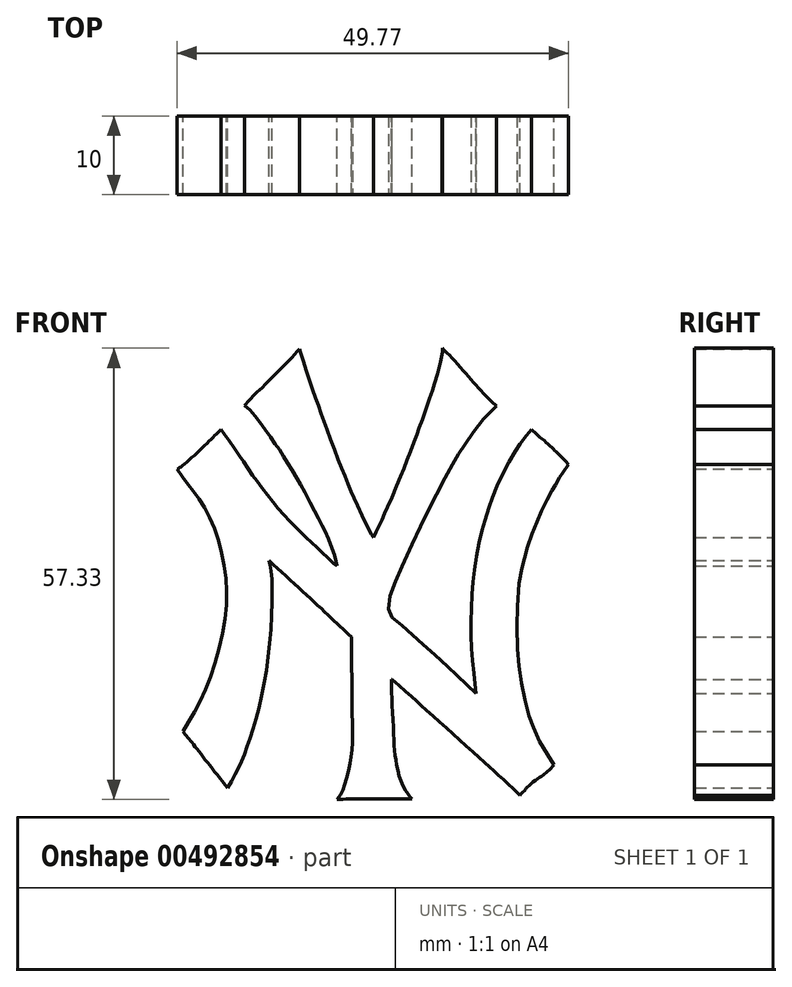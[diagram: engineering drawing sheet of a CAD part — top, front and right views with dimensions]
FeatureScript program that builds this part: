
annotation { "Feature Type Name" : "Feature", "Feature Type Description" : "" }
export const myFeature = defineFeature(function(context is Context, id is Id, definition is map)
    precondition{}
    {
        {
            var Q0;
            Q0=qCreatedBy(makeId("Front.planeOp"),FACE);
            var sketch = newSketch(context, id + "F0", { "sketchPlane" : qUnion([Q0])});
            skFitSpline(sketch, "E0", {"points": [v(5.8, 47.07) * mm, v(6.29, 46.4) * mm, v(7.13, 45.23) * mm, v(8.19, 43.72) * mm, v(8.73, 42.93) * mm, v(9.6, 41.61) * mm, v(10.3, 40.65) * mm, v(11.14, 39.47) * mm, v(12.2, 38.1) * mm, v(13.16, 36.97) * mm, v(14.22, 35.8) * mm, v(15.06, 34.9) * mm, v(15.95, 34) * mm, v(16.93, 33.02) * mm, v(17.78, 32.26) * mm, v(18.71, 31.4) * mm, v(19.49, 30.65) * mm, v(20.36, 29.84) * mm, v(20.56, 29.7) * mm], "startDerivative": vector(7.77, -16.64) * mm, "endDerivative": vector(6.87, -3.56) * mm});
            skFitSpline(sketch, "E1", {"points": [v(20.56, 29.7) * mm, v(20.5, 30.1) * mm, v(20.25, 30.98) * mm, v(19.9, 32.05) * mm, v(19.1, 33.94) * mm, v(18.74, 34.72) * mm, v(18.1, 36) * mm, v(17.32, 37.47) * mm, v(16.13, 39.67) * mm, v(15.54, 40.7) * mm, v(14.54, 42.37) * mm, v(13.92, 43.4) * mm, v(13.19, 44.57) * mm, v(12.51, 45.52) * mm, v(11.5, 47) * mm, v(10.53, 48.24) * mm, v(9.66, 49.36) * mm, v(8.8, 50.14) * mm], "startDerivative": vector(-1.03, 10.89) * mm, "endDerivative": vector(-16.3, 14.17) * mm});
            skFitSpline(sketch, "E2", {"points": [v(8.8, 50.14) * mm, v(9.3, 50.67) * mm, v(10.05, 51.48) * mm, v(11.26, 52.6) * mm, v(13.17, 54.56) * mm, v(14.9, 56.3) * mm, v(15.77, 57.29) * mm, v(15.78, 57.28) * mm], "startDerivative": vector(4.68, 3.9) * mm, "endDerivative": vector(0.38, -0.96) * mm});
            skFitSpline(sketch, "E3", {"points": [v(15.78, 57.28) * mm, v(15.97, 56.7) * mm, v(16.36, 55.47) * mm, v(16.94, 53.7) * mm, v(17.7, 51.47) * mm, v(18.17, 50.1) * mm, v(18.67, 48.69) * mm, v(19.2, 47.22) * mm, v(20.08, 44.92) * mm, v(20.9, 42.77) * mm, v(21.52, 41.23) * mm, v(22.14, 39.73) * mm, v(22.6, 38.62) * mm, v(23.2, 37.29) * mm, v(24.37, 34.84) * mm, v(25.12, 33.43) * mm, v(25.16, 33.38) * mm, v(25.2, 33.37) * mm], "startDerivative": vector(4.56, -13.3) * mm, "endDerivative": vector(1.36, -3.09) * mm});
            skFitSpline(sketch, "E4", {"points": [v(25.2, 33.37) * mm, v(25.59, 34.14) * mm, v(26.08, 35.18) * mm, v(26.53, 36.22) * mm, v(27.1, 37.44) * mm, v(28.39, 40.5) * mm, v(29.14, 42.35) * mm, v(29.9, 44.3) * mm, v(30.64, 46.27) * mm, v(31.03, 47.35) * mm, v(31.94, 49.9) * mm, v(32.7, 52.07) * mm, v(33.1, 53.45) * mm, v(33.91, 56.67) * mm, v(33.91, 57.37) * mm, v(33.92, 57.4) * mm], "startDerivative": vector(7.42, 14.98) * mm, "endDerivative": vector(0.15, 2.07) * mm});
            skFitSpline(sketch, "E5", {"points": [v(33.92, 57.4) * mm, v(34.4, 56.96) * mm, v(35.8, 55.45) * mm, v(37.46, 53.57) * mm, v(38.85, 51.99) * mm, v(40.17, 50.62) * mm, v(40.82, 50.06) * mm], "startDerivative": vector(3.8, -3.56) * mm, "endDerivative": vector(4.92, -3.97) * mm});
            skFitSpline(sketch, "E6", {"points": [v(40.82, 50.06) * mm, v(39.4, 48.66) * mm, v(38.91, 48.1) * mm, v(37.95, 46.84) * mm, v(37.23, 45.77) * mm, v(36.72, 45.03) * mm, v(36.41, 44.52) * mm, v(36.04, 44) * mm, v(35.71, 43.4) * mm, v(35.32, 42.78) * mm, v(34.94, 42.07) * mm, v(34.23, 40.88) * mm, v(33.53, 39.5) * mm, v(32.67, 37.88) * mm, v(32.1, 36.75) * mm, v(31.56, 35.57) * mm, v(30.39, 33.23) * mm, v(29.9, 32.1) * mm, v(28.63, 29.27) * mm, v(28.16, 28.2) * mm, v(27.8, 27.17) * mm, v(27.35, 26.05) * mm, v(27.13, 25.13) * mm, v(27.11, 24.4) * mm, v(27.2, 23.7) * mm, v(27.3, 23.41) * mm, v(27.56, 23.2) * mm, v(28.2, 22.63) * mm, v(28.76, 22.2) * mm, v(29.44, 21.61) * mm, v(30.2, 20.92) * mm, v(31, 20.2) * mm, v(31.66, 19.6) * mm, v(32.57, 18.76) * mm, v(33.62, 17.84) * mm, v(34.6, 16.9) * mm, v(35.32, 16.26) * mm, v(35.8, 15.78) * mm, v(36.48, 15.16) * mm, v(37.11, 14.57) * mm, v(37.7, 14.02) * mm, v(38.2, 13.57) * mm], "startDerivative": vector(-48.5, -47.3) * mm, "endDerivative": vector(24.26, -22.89) * mm});
            skFitSpline(sketch, "E7", {"points": [v(38.2, 13.57) * mm, v(38.2, 13.75) * mm, v(38.08, 14.65) * mm, v(37.97, 15.57) * mm, v(37.88, 16.57) * mm, v(37.75, 17.92) * mm, v(37.68, 18.85) * mm, v(37.6, 20.41) * mm, v(37.59, 21.39) * mm, v(37.57, 23.11) * mm, v(37.6, 24.24) * mm, v(37.68, 25.87) * mm, v(37.76, 26.87) * mm, v(37.91, 28.35) * mm, v(38.02, 29.3) * mm, v(38.24, 30.73) * mm, v(38.47, 31.9) * mm, v(38.82, 33.6) * mm, v(39.06, 34.48) * mm, v(39.25, 35.27) * mm, v(39.57, 36.27) * mm, v(40.06, 37.77) * mm, v(40.23, 38.25) * mm, v(40.61, 39.3) * mm, v(41.18, 40.51) * mm, v(41.92, 42.1) * mm, v(42.36, 42.83) * mm, v(43.07, 44.12) * mm, v(43.43, 44.64) * mm, v(43.68, 45.1) * mm, v(44.05, 45.58) * mm, v(44.62, 46.3) * mm, v(44.95, 46.72) * mm, v(45.26, 47.08) * mm], "startDerivative": vector(0.66, 11.24) * mm, "endDerivative": vector(16.34, 19.47) * mm});
            skFitSpline(sketch, "E8", {"points": [v(45.26, 47.08) * mm, v(45.8, 46.58) * mm, v(46.11, 46.3) * mm, v(46.54, 45.92) * mm, v(46.9, 45.63) * mm, v(47.68, 44.9) * mm, v(48.17, 44.45) * mm, v(48.6, 44.02) * mm, v(49.7, 42.92) * mm, v(49.98, 42.64) * mm], "startDerivative": vector(4.93, -4.84) * mm, "endDerivative": vector(2.7, -2.2) * mm});
            skFitSpline(sketch, "E9", {"points": [v(49.98, 42.64) * mm, v(49.57, 42.05) * mm, v(49.49, 41.95) * mm, v(49.3, 41.66) * mm, v(49.2, 41.52) * mm, v(49.1, 41.4) * mm, v(49.04, 41.3) * mm, v(48.9, 41.09) * mm, v(48.75, 40.88) * mm, v(48.55, 40.53) * mm, v(48.4, 40.28) * mm, v(48.27, 40.02) * mm, v(48.2, 39.9) * mm, v(48.08, 39.72) * mm, v(47.99, 39.53) * mm, v(47.84, 39.3) * mm, v(47.7, 39.03) * mm, v(47.57, 38.79) * mm, v(47.12, 37.93) * mm, v(46.7, 37.06) * mm, v(46.6, 36.81) * mm, v(46.2, 36) * mm, v(46, 35.48) * mm, v(45.88, 35.18) * mm, v(45.62, 34.63) * mm, v(45.28, 33.68) * mm, v(45.15, 33.33) * mm, v(44.8, 32.22) * mm, v(44.57, 31.51) * mm, v(44.4, 30.9) * mm, v(44.26, 30.28) * mm, v(44.16, 29.9) * mm, v(44.06, 29.5) * mm, v(44.05, 29.37) * mm, v(43.75, 27.84) * mm, v(43.61, 26.7) * mm, v(43.46, 23.4) * mm, v(43.44, 22.08) * mm, v(43.48, 19.62) * mm, v(43.53, 18.18) * mm, v(43.7, 16.93) * mm, v(43.86, 15.63) * mm, v(44.1, 14.18) * mm, v(44.37, 12.86) * mm, v(44.66, 11.78) * mm, v(45.02, 10.46) * mm, v(45.25, 9.8) * mm, v(45.48, 9.23) * mm, v(46.02, 7.96) * mm, v(46.34, 7.36) * mm, v(47, 6.18) * mm, v(47.35, 5.61) * mm, v(47.82, 4.88) * mm, v(48.13, 4.48) * mm], "startDerivative": vector(-26.35, -38.9) * mm, "endDerivative": vector(17.83, -21.66) * mm});
            skFitSpline(sketch, "E10", {"points": [v(48.13, 4.48) * mm, v(47.03, 3.37) * mm, v(45.9, 2.62) * mm, v(44.63, 1.56) * mm, v(44.6, 1.54) * mm, v(44.53, 1.39) * mm, v(43.78, 0.6) * mm], "startDerivative": vector(-4.7, -5.23) * mm, "endDerivative": vector(-4.14, -4.97) * mm});
            skFitSpline(sketch, "E11", {"points": [v(43.78, 0.6) * mm, v(43.14, 1.25) * mm, v(41.78, 2.5) * mm, v(40.42, 3.73) * mm, v(39, 5.03) * mm, v(36.57, 7.24) * mm, v(33.94, 9.58) * mm, v(31.5, 11.78) * mm, v(30.01, 13.12) * mm, v(27.55, 15.34) * mm], "startDerivative": vector(-9.1, 7.9) * mm, "endDerivative": vector(-20.15, 18.23) * mm});
            skFitSpline(sketch, "E12", {"points": [v(27.55, 15.34) * mm, v(27.47, 15.34) * mm, v(27.46, 15.34) * mm], "startDerivative": vector(-0.35, 0) * mm, "endDerivative": vector(-0.02, 0) * mm});
            skFitSpline(sketch, "E13", {"points": [v(27.46, 15.34) * mm, v(27.46, 13.82) * mm, v(27.68, 10.03) * mm, v(27.8, 6.77) * mm, v(28.04, 4.95) * mm, v(28.62, 2.57) * mm, v(29.53, 0.78) * mm, v(30.09, 0.15) * mm], "startDerivative": vector(-0.2, -11.1) * mm, "endDerivative": vector(6.07, -5.96) * mm});
            skFitSpline(sketch, "E14", {"points": [v(30.09, 0.15) * mm, v(28.44, 0.15) * mm, v(26.75, 0.15) * mm, v(22.93, 0.15) * mm, v(20.57, 0.06) * mm], "startDerivative": vector(-8.05, 0) * mm, "endDerivative": vector(-8.4, -0.44) * mm});
            skFitSpline(sketch, "E15", {"points": [v(20.57, 0.06) * mm, v(21.2, 1.07) * mm, v(21.59, 2.07) * mm, v(22.15, 4.17) * mm, v(22.4, 5.96) * mm, v(22.54, 7.86) * mm, v(22.5, 9.42) * mm, v(22.49, 12.08) * mm, v(22.48, 14.2) * mm, v(22.43, 16.05) * mm, v(22.42, 17.88) * mm, v(22.38, 20.7) * mm], "startDerivative": vector(9.5, 14.2) * mm, "endDerivative": vector(-0.52, 26.71) * mm});
            skFitSpline(sketch, "E16", {"points": [v(22.38, 20.7) * mm, v(18.6, 24.26) * mm, v(11.9, 30.45) * mm], "startDerivative": vector(-8.14, 7.71) * mm, "endDerivative": vector(-12.46, 11.62) * mm});
            skFitSpline(sketch, "E17", {"points": [v(6.66, 1.53) * mm, v(2.42, 6.9) * mm, v(0.97, 8.73) * mm], "startDerivative": vector(-7.64, 9.48) * mm, "endDerivative": vector(-3.4, 4.3) * mm});
            skFitSpline(sketch, "E18", {"points": [v(5.8, 47.07) * mm, v(3.97, 45.25) * mm, v(0.78, 42.35) * mm, v(0.2, 42.02) * mm], "startDerivative": vector(-4.36, -4.42) * mm, "endDerivative": vector(-2.5, -1.08) * mm});
            skFitSpline(sketch, "E19", {"points": [v(0.2, 42.02) * mm, v(1.8, 39.84) * mm, v(3.35, 37.77) * mm, v(5.07, 34.24) * mm, v(6.29, 29.33) * mm, v(6.45, 24.04) * mm, v(5.08, 17.39) * mm, v(3, 12.16) * mm, v(0.97, 8.73) * mm], "startDerivative": vector(16.22, -22.8) * mm, "endDerivative": vector(-17.4, -27.22) * mm});
            skFitSpline(sketch, "E20", {"points": [v(6.66, 1.53) * mm, v(8.07, 4.13) * mm, v(9.2, 6.98) * mm, v(10.8, 12.34) * mm, v(12.12, 21.3) * mm, v(12.22, 28.78) * mm, v(11.9, 30.45) * mm], "startDerivative": vector(11.2, 19.5) * mm, "endDerivative": vector(-3.66, 13.4) * mm});
            skSolve(sketch);
        }
        {
            var Q0;
            Q0=qSketchRegion(id+"F0",true);
            extrude(context, id + "F1", {"entities" : qUnion([Q0]), "depth" : 10 * mm, "offsetDistance" : 25 * mm});
        }
    });
